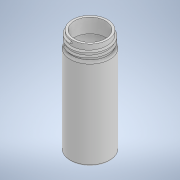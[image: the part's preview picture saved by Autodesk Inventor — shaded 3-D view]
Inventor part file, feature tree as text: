
AUTODESK INVENTOR PART (.ipt)
format: ipt  version: 2022 (Build 260153000, 153)  size: 238,080 bytes
history: native  units: mm
features: sketch x5, extrude x2, fillet x2, revolve x1, sweep x1, chamfer x1, other x1
ambient origin geometry x8: Origin, YZ Plane, XZ Plane, XY Plane, X Axis, Y Axis, Z Axis, Center Point
bodies: Solid1 (feature_tree)
feature tree (13):
  extrude  "Extrusion2"  Depth=1.5mm
  extrude  "Extrusion3"  Depth=1.5mm
  fillet  "Fillet3"  Radius=11.0mm
  revolve  "Revolution1"  Angle=90.0deg
  sweep  "Sweep1"
  chamfer  "Chamfer1"  Distance=1.0mm
  sketch  "Sketch2"  dims[d4=24.5mm d5=1.5mm]
  sketch  "Sketch3"  dims[d6=11.0mm d7=0.0mm d8=1.5mm d9=11.0mm d10=0.0mm]
  sketch  "Sketch4"  dims[d11=1.0mm d12=90.0deg]
  sketch  "Sketch5"  dims[d13=45.0deg d15=1.0mm d16=1.0mm d21=1.0mm d22=1.0mm d23=3.0mm d24=21.0mm d25=24.5mm d26=0.0mm d27=0.0mm d28=0.0mm d29=0.7mm d30=2.0mm d31=45.0deg]
  sketch  "3D Sketch2"
  other  "Helical Curve2"
  fillet  "Fillet1"  Radius=1.0mm
